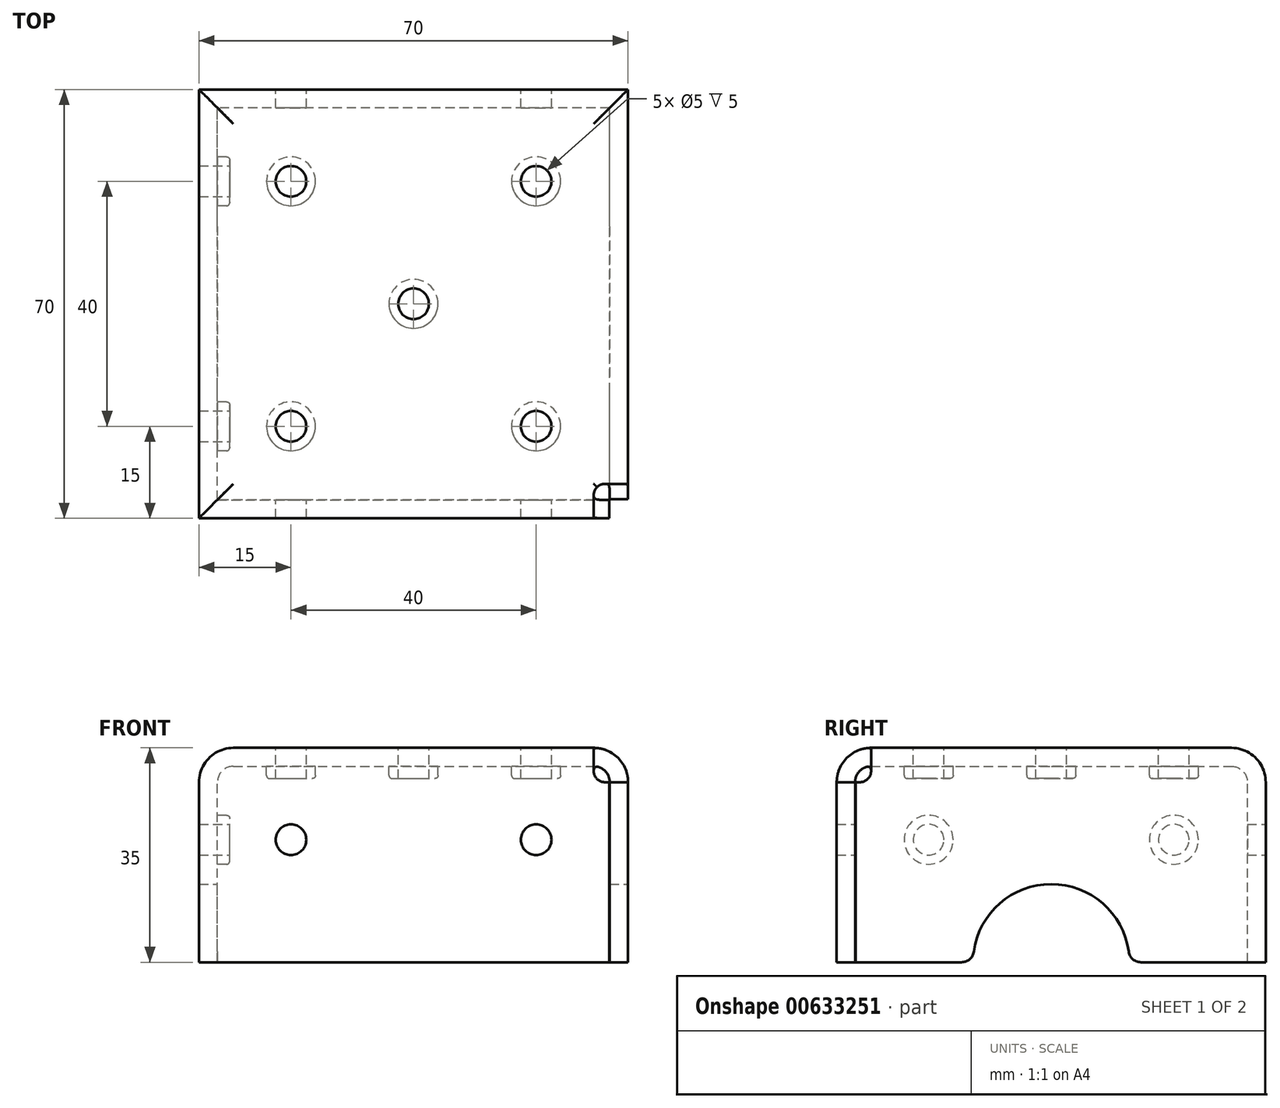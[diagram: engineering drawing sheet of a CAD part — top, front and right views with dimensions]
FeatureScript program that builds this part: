
annotation { "Feature Type Name" : "Feature", "Feature Type Description" : "" }
export const myFeature = defineFeature(function(context is Context, id is Id, definition is map)
    precondition{}
    {
        {
            var Q0;
            Q0=qCreatedBy(makeId("Top.planeOp"),FACE);
            var sketch = newSketch(context, id + "F0", { "sketchPlane" : qUnion([Q0])});
            skLineSegment(sketch, "E0.bottom", {"start": v(35, -35) * mm, "end": v(-35, -35) * mm});
            skLineSegment(sketch, "E0.top", {"start": v(35, 35) * mm, "end": v(-35, 35) * mm});
            skLineSegment(sketch, "E0.left", {"start": v(35, -35) * mm, "end": v(35, 35) * mm});
            skLineSegment(sketch, "E0.right", {"start": v(-35, -35) * mm, "end": v(-35, 35) * mm});
            skPoint(sketch, "E0.middle", {"position": v(0, 0) * mm});
            skSolve(sketch);
        }
        {
            var Q0;
            Q0=qSketchRegion(id+"F0",true);
            extrude(context, id + "F1", {"entities" : qUnion([Q0]), "oppositeDirection" : true, "depth" : 35 * mm});
        }
        {
            var Q0;
            Q0=makeQuery(id+"F1.opExtrude","CAP_EDGE",EDGE,{"disambiguationData":[OSD([sQuery(id+"F0.wireOp",EDGE,"E0.bottom")])],"isStart":true});
            var Q1;
            Q1=makeQuery(id+"F1.opExtrude","CAP_EDGE",EDGE,{"disambiguationData":[OSD([sQuery(id+"F0.wireOp",EDGE,"E0.left")])],"isStart":true});
            var Q2;
            Q2=makeQuery(id+"F1.opExtrude","CAP_EDGE",EDGE,{"disambiguationData":[OSD([sQuery(id+"F0.wireOp",EDGE,"E0.top")])],"isStart":true});
            var Q3;
            Q3=makeQuery(id+"F1.opExtrude","CAP_EDGE",EDGE,{"disambiguationData":[OSD([sQuery(id+"F0.wireOp",EDGE,"E0.right")])],"isStart":true});
            fillet(context, id + "F2", {"entities" : qUnion([Q0, Q1, Q2, Q3]), "radius" : 5.6 * mm, "tangentPropagation" : true, "allowEdgeOverflow" : false});
        }
        {
            var Q0;
            Q0=makeQuery(id+"F1.opExtrude","CAP_FACE",FACE,{"disambiguationData":[OSD([sQuery(id+"F0.wireOp",EDGE,"E0.bottom"),sQuery(id+"F0.wireOp",EDGE,"E0.top"),sQuery(id+"F0.wireOp",EDGE,"E0.left"),sQuery(id+"F0.wireOp",EDGE,"E0.right")])],"isStart":false});
            shell(context, id + "F3", {"entities" : qUnion([Q0]), "thickness" : 3 * mm});
        }
        {
            var Q0;
            Q0=makeQuery(id+"F1.opExtrude","CAP_FACE",FACE,{"disambiguationData":[OSD([sQuery(id+"F0.wireOp",EDGE,"E0.bottom"),sQuery(id+"F0.wireOp",EDGE,"E0.top"),sQuery(id+"F0.wireOp",EDGE,"E0.left"),sQuery(id+"F0.wireOp",EDGE,"E0.right")])],"isStart":false});
            var sketch = newSketch(context, id + "F4", { "sketchPlane" : qUnion([Q0])});
            skLineSegment(sketch, "E1.bottom", {"start": v(35, 35) * mm, "end": v(31.9, 35) * mm});
            skLineSegment(sketch, "E1.top", {"start": v(35, 31.9) * mm, "end": v(31.9, 31.9) * mm});
            skLineSegment(sketch, "E1.left", {"start": v(35, 35) * mm, "end": v(35, 31.9) * mm});
            skLineSegment(sketch, "E1.right", {"start": v(31.9, 35) * mm, "end": v(31.9, 31.9) * mm});
            skSolve(sketch);
        }
        {
            var Q0;
            Q0=qSketchRegion(id+"F4",true);
            extrude(context, id + "F5", {"entities" : qUnion([Q0]), "operationType" : NewBodyOperationType.REMOVE, "oppositeDirection" : true, "depth" : 38.4 * mm});
        }
        {
            var Q0;
            Q0=makeQuery(id+"F1.opExtrude","CAP_FACE",FACE,{"disambiguationData":[OSD([sQuery(id+"F0.wireOp",EDGE,"E0.bottom"),sQuery(id+"F0.wireOp",EDGE,"E0.top"),sQuery(id+"F0.wireOp",EDGE,"E0.left"),sQuery(id+"F0.wireOp",EDGE,"E0.right")])],"isStart":true});
            var sketch = newSketch(context, id + "F6", { "sketchPlane" : qUnion([Q0])});
            skLineSegment(sketch, "E2.bottom", {"start": v(29.4, -29.4) * mm, "end": v(35, -29.4) * mm});
            skLineSegment(sketch, "E2.top", {"start": v(29.4, -35) * mm, "end": v(35, -35) * mm});
            skLineSegment(sketch, "E2.left", {"start": v(29.4, -29.4) * mm, "end": v(29.4, -35) * mm});
            skLineSegment(sketch, "E2.right", {"start": v(35, -29.4) * mm, "end": v(35, -35) * mm});
            skSolve(sketch);
        }
        {
            var Q0;
            Q0=makeQuery(id+"F6.imprint","IMPRINT",FACE,{"disambiguationData":[TD([[makeQuery(id+"F6.imprint","IMPRINT",EDGE,{"derivedFrom":sQuery(id+"F6.wireOp",EDGE,"E2.bottom")}),-1.0]])]});
            extrude(context, id + "F7", {"entities" : qUnion([Q0]), "operationType" : NewBodyOperationType.REMOVE, "oppositeDirection" : true, "depth" : 5.6 * mm});
        }
        {
            var Q0;
            Q0=makeQuery(id+"F7.boolean.opBoolean","COPY",EDGE,{"derivedFrom":makeQuery(id+"F7.opExtrude","SWEPT_EDGE",EDGE,{"disambiguationData":[OSD([sQuery(id+"F0.wireOp",EDGE,"E0.bottom"),sQuery(id+"F0.wireOp",EDGE,"E0.top"),sQuery(id+"F0.wireOp",EDGE,"E0.left"),sQuery(id+"F0.wireOp",EDGE,"E0.right"),sQuery(id+"F6.wireOp",EDGE,"E2.bottom"),sQuery(id+"F6.wireOp",EDGE,"E2.left")])]})});
            var Q1;
            Q1=makeQuery(id+"F7.boolean.opBoolean","COPY",EDGE,{"derivedFrom":makeQuery(id+"F7.opExtrude","CAP_EDGE",EDGE,{"disambiguationData":[OSD([sQuery(id+"F6.wireOp",EDGE,"E2.bottom")])],"isStart":false})});
            var Q2;
            Q2=makeQuery(id+"F7.boolean.opBoolean","COPY",EDGE,{"derivedFrom":makeQuery(id+"F7.opExtrude","CAP_EDGE",EDGE,{"disambiguationData":[OSD([sQuery(id+"F6.wireOp",EDGE,"E2.left")])],"isStart":false})});
            fillet(context, id + "F8", {"entities" : qUnion([Q0, Q1, Q2]), "radius" : 1.8 * mm, "tangentPropagation" : true, "allowEdgeOverflow" : false});
        }
        {
            var Q0;
            Q0=makeQuery(id+"F3.opShell","OFFSET_FACE",FACE,{"disambiguationData":[OSD([sQuery(id+"F0.wireOp",EDGE,"E0.bottom"),sQuery(id+"F0.wireOp",EDGE,"E0.top"),sQuery(id+"F0.wireOp",EDGE,"E0.left"),sQuery(id+"F0.wireOp",EDGE,"E0.right")])]});
            var sketch = newSketch(context, id + "F9", { "sketchPlane" : qUnion([Q0])});
            skCircle(sketch, "E3", {"center": v(-20, 20) * mm, "radius": 4 * mm});
            skLineSegment(sketch, "E4.bottom", {"start": v(-20, 20) * mm, "end": v(20, 20) * mm, "construction": true});
            skLineSegment(sketch, "E4.top", {"start": v(-20, -20) * mm, "end": v(20, -20) * mm, "construction": true});
            skLineSegment(sketch, "E4.left", {"start": v(-20, 20) * mm, "end": v(-20, -20) * mm, "construction": true});
            skLineSegment(sketch, "E4.right", {"start": v(20, 20) * mm, "end": v(20, -20) * mm, "construction": true});
            skPoint(sketch, "E4.middle", {"position": v(0, 0) * mm});
            skCircle(sketch, "E5", {"center": v(-20, -20) * mm, "radius": 4 * mm});
            skCircle(sketch, "E6", {"center": v(20, -20) * mm, "radius": 4 * mm});
            skCircle(sketch, "E7", {"center": v(20, 20) * mm, "radius": 4 * mm});
            skCircle(sketch, "E8", {"center": v(0, 0) * mm, "radius": 4 * mm});
            skSolve(sketch);
        }
        {
            var Q0;
            Q0=makeQuery(id+"F9.imprint","IMPRINT",FACE,{"disambiguationData":[TD([[makeQuery(id+"F9.imprint","IMPRINT",EDGE,{"derivedFrom":sQuery(id+"F9.wireOp",EDGE,"E5")}),1.0]])]});
            var Q1;
            Q1=makeQuery(id+"F9.imprint","IMPRINT",FACE,{"disambiguationData":[TD([[makeQuery(id+"F9.imprint","IMPRINT",EDGE,{"derivedFrom":sQuery(id+"F9.wireOp",EDGE,"E6")}),1.0]])]});
            var Q2;
            Q2=makeQuery(id+"F9.imprint","IMPRINT",FACE,{"disambiguationData":[TD([[makeQuery(id+"F9.imprint","IMPRINT",EDGE,{"derivedFrom":sQuery(id+"F9.wireOp",EDGE,"E7")}),1.0]])]});
            var Q3;
            Q3=makeQuery(id+"F9.imprint","IMPRINT",FACE,{"disambiguationData":[TD([[makeQuery(id+"F9.imprint","IMPRINT",EDGE,{"derivedFrom":sQuery(id+"F9.wireOp",EDGE,"E3")}),1.0]])]});
            var Q4;
            Q4=makeQuery(id+"F9.imprint","IMPRINT",FACE,{"disambiguationData":[TD([[makeQuery(id+"F9.imprint","IMPRINT",EDGE,{"derivedFrom":sQuery(id+"F9.wireOp",EDGE,"E8")}),1.0]])]});
            extrude(context, id + "F10", {"entities" : qUnion([Q0, Q1, Q2, Q3, Q4]), "operationType" : NewBodyOperationType.ADD, "depth" : 2 * mm});
        }
        {
            var Q0;
            Q0=makeQuery(id+"F10.opExtrude","CAP_EDGE",EDGE,{"disambiguationData":[OSD([sQuery(id+"F9.wireOp",EDGE,"E3")])],"isStart":false});
            var Q1;
            Q1=makeQuery(id+"F10.opExtrude","CAP_EDGE",EDGE,{"disambiguationData":[OSD([sQuery(id+"F9.wireOp",EDGE,"E3")])],"isStart":true});
            var Q2;
            Q2=makeQuery(id+"F10.opExtrude","CAP_FACE",FACE,{"disambiguationData":[OSD([sQuery(id+"F9.wireOp",EDGE,"E5")])],"isStart":false});
            var Q3;
            Q3=makeQuery(id+"F10.opExtrude","CAP_FACE",FACE,{"disambiguationData":[OSD([sQuery(id+"F9.wireOp",EDGE,"E6")])],"isStart":false});
            var Q4;
            Q4=makeQuery(id+"F10.opExtrude","CAP_FACE",FACE,{"disambiguationData":[OSD([sQuery(id+"F9.wireOp",EDGE,"E7")])],"isStart":false});
            var Q5;
            Q5=makeQuery(id+"F10.opExtrude","CAP_EDGE",EDGE,{"disambiguationData":[OSD([sQuery(id+"F9.wireOp",EDGE,"E5")])],"isStart":true});
            var Q6;
            Q6=makeQuery(id+"F10.opExtrude","CAP_EDGE",EDGE,{"disambiguationData":[OSD([sQuery(id+"F9.wireOp",EDGE,"E6")])],"isStart":true});
            var Q7;
            Q7=makeQuery(id+"F10.opExtrude","CAP_EDGE",EDGE,{"disambiguationData":[OSD([sQuery(id+"F9.wireOp",EDGE,"E7")])],"isStart":true});
            var Q8;
            Q8=makeQuery(id+"F10.opExtrude","CAP_EDGE",EDGE,{"disambiguationData":[OSD([sQuery(id+"F9.wireOp",EDGE,"E8")])],"isStart":true});
            var Q9;
            Q9=makeQuery(id+"F10.opExtrude","CAP_EDGE",EDGE,{"disambiguationData":[OSD([sQuery(id+"F9.wireOp",EDGE,"E8")])],"isStart":false});
            fillet(context, id + "F11", {"entities" : qUnion([Q0, Q1, Q2, Q3, Q4, Q5, Q6, Q7, Q8, Q9]), "radius" : 0.5 * mm, "tangentPropagation" : true, "allowEdgeOverflow" : false});
        }
        {
            var Q0;
            Q0=makeQuery(id+"F1.opExtrude","CAP_FACE",FACE,{"disambiguationData":[OSD([sQuery(id+"F0.wireOp",EDGE,"E0.bottom"),sQuery(id+"F0.wireOp",EDGE,"E0.top"),sQuery(id+"F0.wireOp",EDGE,"E0.left"),sQuery(id+"F0.wireOp",EDGE,"E0.right")])],"isStart":true});
            var sketch = newSketch(context, id + "F12", { "sketchPlane" : qUnion([Q0])});
            skCircle(sketch, "E9.0", {"center": v(-20, -20) * mm, "radius": 3.5 * mm, "construction": true});
            skCircle(sketch, "E10.0", {"center": v(-20, 20) * mm, "radius": 3.5 * mm, "construction": true});
            skCircle(sketch, "E11.0", {"center": v(20, 20) * mm, "radius": 3.5 * mm, "construction": true});
            skCircle(sketch, "E12.0", {"center": v(20, -20) * mm, "radius": 3.5 * mm, "construction": true});
            skCircle(sketch, "E13.0", {"center": v(0, 0) * mm, "radius": 3.5 * mm, "construction": true});
            skSolve(sketch);
        }
        {
            var Q0;
            Q0=sQuery(id+"F12.wireOp",VERTEX,"E9.0.center");
            var Q1;
            Q1=sQuery(id+"F12.wireOp",VERTEX,"E10.0.center");
            var Q2;
            Q2=sQuery(id+"F12.wireOp",VERTEX,"E11.0.center");
            var Q3;
            Q3=sQuery(id+"F12.wireOp",VERTEX,"E13.0.center");
            var Q4;
            Q4=sQuery(id+"F12.wireOp",VERTEX,"E12.0.center");
            var Q5;
            Q5=makeQuery(id+"F1.opExtrude","SWEPT_BODY",BODY,{"disambiguationData":[OSD([sQuery(id+"F0.wireOp",EDGE,"E0.bottom"),sQuery(id+"F0.wireOp",EDGE,"E0.top"),sQuery(id+"F0.wireOp",EDGE,"E0.left"),sQuery(id+"F0.wireOp",EDGE,"E0.right")])]});
            hole(context, id + "F13", {"style" : HoleStyle.SIMPLE, "endStyle" : HoleEndStyle.THROUGH, "standardTappedOrClearance" : lookupTablePath({ "standard" : "ISO", "engagement" : "75%", "pitch" : "1 mm", "size" : "M6", "type" : "Tapped" }), "standardBlindInLast" : lookupTablePath({ "standard" : "ISO", "engagement" : "75%", "pitch" : "1 mm", "size" : "M6", "type" : "Tapped" }), "holeDiameter" : 5 * mm, "locations" : qUnion([Q0, Q1, Q2, Q3, Q4]), "scope" : qUnion([Q5]), "isTappedThrough" : true, "majorDiameter" : 6 * mm, "showTappedDepth" : true});
        }
        {
            var Q0;
            {var subQ0=sQuery(id+"F0.wireOp",EDGE,"E0.right");Q0=makeQuery(id+"F3.opShell","OFFSET_FACE",FACE,{"disambiguationData":[OSD([subQ0]),TDD([makeQuery(id+"F1.opExtrude","SWEPT_FACE",FACE,{"disambiguationData":[OSD([subQ0])]})])]});}
            var sketch = newSketch(context, id + "F14", { "sketchPlane" : qUnion([Q0])});
            skCircle(sketch, "E14", {"center": v(-20, -15) * mm, "radius": 4 * mm});
            skCircle(sketch, "E15", {"center": v(20, -15) * mm, "radius": 4 * mm});
            skSolve(sketch);
        }
        {
            var Q0;
            Q0=qSketchRegion(id+"F14",true);
            extrude(context, id + "F15", {"entities" : qUnion([Q0]), "operationType" : NewBodyOperationType.ADD, "depth" : 2 * mm});
        }
        {
            var Q0;
            Q0=makeQuery(id+"F15.opExtrude","CAP_EDGE",EDGE,{"disambiguationData":[OSD([sQuery(id+"F14.wireOp",EDGE,"E14")])],"isStart":false});
            var Q1;
            Q1=makeQuery(id+"F15.opExtrude","CAP_EDGE",EDGE,{"disambiguationData":[OSD([sQuery(id+"F14.wireOp",EDGE,"E15")])],"isStart":false});
            var Q2;
            Q2=makeQuery(id+"F15.opExtrude","CAP_EDGE",EDGE,{"disambiguationData":[OSD([sQuery(id+"F14.wireOp",EDGE,"E15")])],"isStart":true});
            var Q3;
            Q3=makeQuery(id+"F15.opExtrude","CAP_EDGE",EDGE,{"disambiguationData":[OSD([sQuery(id+"F14.wireOp",EDGE,"E14")])],"isStart":true});
            fillet(context, id + "F16", {"entities" : qUnion([Q0, Q1, Q2, Q3]), "radius" : 0.5 * mm, "tangentPropagation" : true, "allowEdgeOverflow" : false});
        }
        {
            var Q0;
            Q0=makeQuery(id+"F15.opExtrude","CAP_FACE",FACE,{"disambiguationData":[OSD([sQuery(id+"F14.wireOp",EDGE,"E14")])],"isStart":false});
            var sketch = newSketch(context, id + "F17", { "sketchPlane" : qUnion([Q0])});
            skPoint(sketch, "E16", {"position": v(-20, -15) * mm});
            skPoint(sketch, "E17", {"position": v(20, -15) * mm});
            skSolve(sketch);
        }
        {
            var Q0;
            Q0=sQuery(id+"F17.wireOp",VERTEX,"E16");
            var Q1;
            Q1=sQuery(id+"F17.wireOp",VERTEX,"E17");
            var Q2;
            Q2=makeQuery(id+"F1.opExtrude","SWEPT_BODY",BODY,{"disambiguationData":[OSD([sQuery(id+"F0.wireOp",EDGE,"E0.bottom"),sQuery(id+"F0.wireOp",EDGE,"E0.top"),sQuery(id+"F0.wireOp",EDGE,"E0.left"),sQuery(id+"F0.wireOp",EDGE,"E0.right")])]});
            hole(context, id + "F18", {"style" : HoleStyle.SIMPLE, "endStyle" : HoleEndStyle.THROUGH, "standardTappedOrClearance" : lookupTablePath({ "standard" : "ISO", "engagement" : "75%", "pitch" : "1 mm", "size" : "M6", "type" : "Tapped" }), "standardBlindInLast" : lookupTablePath({ "standard" : "ISO", "engagement" : "75%", "pitch" : "1 mm", "size" : "M6", "type" : "Tapped" }), "holeDiameter" : 5 * mm, "locations" : qUnion([Q0, Q1]), "scope" : qUnion([Q2]), "isTappedThrough" : true, "majorDiameter" : 6 * mm, "showTappedDepth" : true});
        }
        {
            var Q0;
            Q0=makeQuery(id+"F1.opExtrude","SWEPT_FACE",FACE,{"disambiguationData":[OSD([sQuery(id+"F0.wireOp",EDGE,"E0.top")])]});
            var sketch = newSketch(context, id + "F19", { "sketchPlane" : qUnion([Q0])});
            skPoint(sketch, "E18", {"position": v(-20, -15) * mm});
            skPoint(sketch, "E19", {"position": v(20, -15) * mm});
            skSolve(sketch);
        }
        {
            var Q0;
            Q0=sQuery(id+"F19.wireOp",VERTEX,"E19");
            var Q1;
            Q1=sQuery(id+"F19.wireOp",VERTEX,"E18");
            var Q2;
            Q2=makeQuery(id+"F1.opExtrude","SWEPT_BODY",BODY,{"disambiguationData":[OSD([sQuery(id+"F0.wireOp",EDGE,"E0.bottom"),sQuery(id+"F0.wireOp",EDGE,"E0.top"),sQuery(id+"F0.wireOp",EDGE,"E0.left"),sQuery(id+"F0.wireOp",EDGE,"E0.right")])]});
            hole(context, id + "F20", {"style" : HoleStyle.SIMPLE, "endStyle" : HoleEndStyle.THROUGH, "standardTappedOrClearance" : lookupTablePath({ "standard" : "ISO", "engagement" : "75%", "pitch" : "1 mm", "size" : "M6", "type" : "Tapped" }), "standardBlindInLast" : lookupTablePath({ "standard" : "ISO", "engagement" : "75%", "pitch" : "1 mm", "size" : "M6", "type" : "Tapped" }), "holeDiameter" : 5 * mm, "locations" : qUnion([Q0, Q1]), "scope" : qUnion([Q2]), "isTappedThrough" : true, "majorDiameter" : 6 * mm, "showTappedDepth" : true});
        }
        {
            var Q0;
            Q0=makeQuery(id+"F1.opExtrude","SWEPT_FACE",FACE,{"disambiguationData":[OSD([sQuery(id+"F0.wireOp",EDGE,"E0.bottom")])]});
            var sketch = newSketch(context, id + "F21", { "sketchPlane" : qUnion([Q0])});
            skCircle(sketch, "E20", {"center": v(0, -35) * mm, "radius": 15.25 * mm});
            skSolve(sketch);
        }
        {
            var Q0;
            {var subQ0=sQuery(id+"F21.wireOp",EDGE,"E20");var subQ1=makeQuery(id+"F1.opExtrude","CAP_EDGE",EDGE,{"disambiguationData":[OSD([sQuery(id+"F0.wireOp",EDGE,"E0.bottom")])],"isStart":false});var subQ2=makeQuery(id+"F21.imprint","INTERSECT",VERTEX,{"disambiguationData":[OD(0.0)],"derivedFrom":[subQ1,subQ0]});Q0=makeQuery(id+"F21.imprint","IMPRINT",FACE,{"disambiguationData":[TD([[makeQuery(id+"F21.imprint","IMPRINT",EDGE,{"disambiguationData":[TD([[subQ2,-1.0]])],"derivedFrom":subQ0}),1.0]])]});}
            extrude(context, id + "F22", {"entities" : qUnion([Q0]), "operationType" : NewBodyOperationType.REMOVE, "endBound" : BoundingType.THROUGH_ALL, "oppositeDirection" : true, "depth" : 25 * mm});
        }
        {
            var Q0;
            Q0=makeQuery(id+"F1.opExtrude","SWEPT_FACE",FACE,{"disambiguationData":[OSD([sQuery(id+"F0.wireOp",EDGE,"E0.left")])]});
            var sketch = newSketch(context, id + "F23", { "sketchPlane" : qUnion([Q0])});
            skCircle(sketch, "E21", {"center": v(0, -35) * mm, "radius": 12.75 * mm});
            skSolve(sketch);
        }
        {
            var Q0;
            Q0=qSketchRegion(id+"F23",true);
            extrude(context, id + "F24", {"entities" : qUnion([Q0]), "operationType" : NewBodyOperationType.REMOVE, "endBound" : BoundingType.THROUGH_ALL, "oppositeDirection" : true, "depth" : 25 * mm});
        }
        {
            var Q0;
            {var subQ0=sQuery(id+"F0.wireOp",EDGE,"E0.bottom");var subQ1=makeQuery(id+"F1.opExtrude","SWEPT_FACE",FACE,{"disambiguationData":[OSD([subQ0])]});var subQ2=sQuery(id+"F21.wireOp",EDGE,"E20");Q0=makeQuery(id+"F22.boolean.opBoolean","COPY",EDGE,{"disambiguationData":[TD([subQ1])],"derivedFrom":makeQuery(id+"F22.opExtrude","SWEPT_EDGE",EDGE,{"disambiguationData":[OSD([subQ0,subQ2]),TDD([makeQuery(id+"F21.imprint","INTERSECT",VERTEX,{"disambiguationData":[OD(0.0)],"derivedFrom":[makeQuery(id+"F1.opExtrude","CAP_EDGE",EDGE,{"disambiguationData":[OSD([subQ0])],"isStart":false}),subQ2]})])]})});}
            var Q1;
            {var subQ0=sQuery(id+"F0.wireOp",EDGE,"E0.bottom");var subQ1=makeQuery(id+"F1.opExtrude","SWEPT_FACE",FACE,{"disambiguationData":[OSD([subQ0])]});var subQ2=sQuery(id+"F21.wireOp",EDGE,"E20");Q1=makeQuery(id+"F22.boolean.opBoolean","COPY",EDGE,{"disambiguationData":[TD([subQ1])],"derivedFrom":makeQuery(id+"F22.opExtrude","SWEPT_EDGE",EDGE,{"disambiguationData":[OSD([subQ0,subQ2]),TDD([makeQuery(id+"F21.imprint","INTERSECT",VERTEX,{"disambiguationData":[OD(1.0)],"derivedFrom":[makeQuery(id+"F1.opExtrude","CAP_EDGE",EDGE,{"disambiguationData":[OSD([subQ0])],"isStart":false}),subQ2]})])]})});}
            var Q2;
            {var subQ0=sQuery(id+"F0.wireOp",EDGE,"E0.right");var subQ1=makeQuery(id+"F1.opExtrude","SWEPT_FACE",FACE,{"disambiguationData":[OSD([subQ0])]});var subQ6=sQuery(id+"F0.wireOp",EDGE,"E0.top");var subQ7=makeQuery(id+"F1.opExtrude","SWEPT_FACE",FACE,{"disambiguationData":[OSD([subQ6])]});var subQ9=sQuery(id+"F0.wireOp",EDGE,"E0.left");Q2=makeQuery(id+"F24.boolean.opBoolean","INTERSECT",EDGE,{"disambiguationData":[OD(0.0)],"derivedFrom":[makeQuery(id+"Fg5Al07xBOhborq_1.1.FdxJJ5X4k0Y0wya_1.1.F5.boolean.opBoolean","SPLIT",FACE,{"disambiguationData":[TD([subQ1])],"derivedFrom":makeQuery(id+"Fg5Al07xBOhborq_1.1.F5.boolean.opBoolean","SPLIT",FACE,{"disambiguationData":[TD([subQ7])],"derivedFrom":makeQuery(id+"FdxJJ5X4k0Y0wya_1.1.F5.boolean.opBoolean","SPLIT",FACE,{"disambiguationData":[TD([subQ7])],"derivedFrom":makeQuery(id+"F1.opExtrude","CAP_FACE",FACE,{"disambiguationData":[OSD([sQuery(id+"F0.wireOp",EDGE,"E0.bottom"),subQ6,subQ9,subQ0])],"isStart":false})})})}),makeQuery(id+"F24.opExtrude","SWEPT_FACE",FACE,{"disambiguationData":[OSD([sQuery(id+"F23.wireOp",EDGE,"E21")])]})]});}
            var Q3;
            {var subQ0=sQuery(id+"F0.wireOp",EDGE,"E0.right");var subQ1=makeQuery(id+"F1.opExtrude","SWEPT_FACE",FACE,{"disambiguationData":[OSD([subQ0])]});var subQ6=sQuery(id+"F0.wireOp",EDGE,"E0.top");var subQ7=makeQuery(id+"F1.opExtrude","SWEPT_FACE",FACE,{"disambiguationData":[OSD([subQ6])]});var subQ9=sQuery(id+"F0.wireOp",EDGE,"E0.left");Q3=makeQuery(id+"F24.boolean.opBoolean","INTERSECT",EDGE,{"disambiguationData":[OD(1.0)],"derivedFrom":[makeQuery(id+"Fg5Al07xBOhborq_1.1.FdxJJ5X4k0Y0wya_1.1.F5.boolean.opBoolean","SPLIT",FACE,{"disambiguationData":[TD([subQ1])],"derivedFrom":makeQuery(id+"Fg5Al07xBOhborq_1.1.F5.boolean.opBoolean","SPLIT",FACE,{"disambiguationData":[TD([subQ7])],"derivedFrom":makeQuery(id+"FdxJJ5X4k0Y0wya_1.1.F5.boolean.opBoolean","SPLIT",FACE,{"disambiguationData":[TD([subQ7])],"derivedFrom":makeQuery(id+"F1.opExtrude","CAP_FACE",FACE,{"disambiguationData":[OSD([sQuery(id+"F0.wireOp",EDGE,"E0.bottom"),subQ6,subQ9,subQ0])],"isStart":false})})})}),makeQuery(id+"F24.opExtrude","SWEPT_FACE",FACE,{"disambiguationData":[OSD([sQuery(id+"F23.wireOp",EDGE,"E21")])]})]});}
            var Q4;
            Q4=makeQuery(id+"Fg5Al07xBOhborq_1.1.FdxJJ5X4k0Y0wya_1.1.F5.boolean.opBoolean","COPY",EDGE,{"derivedFrom":makeQuery(id+"Fg5Al07xBOhborq_1.1.FdxJJ5X4k0Y0wya_1.1.F5.opExtrude","CAP_EDGE",EDGE,{"disambiguationData":[OSD([sQuery(id+"F4.wireOp",EDGE,"E1.top")])],"isStart":true})});
            var Q5;
            Q5=makeQuery(id+"Fg5Al07xBOhborq_1.1.FdxJJ5X4k0Y0wya_1.1.F5.boolean.opBoolean","COPY",EDGE,{"derivedFrom":makeQuery(id+"Fg5Al07xBOhborq_1.1.FdxJJ5X4k0Y0wya_1.1.F5.opExtrude","CAP_EDGE",EDGE,{"disambiguationData":[OSD([sQuery(id+"F4.wireOp",EDGE,"E1.right")])],"isStart":true})});
            var Q6;
            {var subQ0=sQuery(id+"F0.wireOp",EDGE,"E0.top");var subQ1=sQuery(id+"F0.wireOp",EDGE,"E0.bottom");var subQ2=makeQuery(id+"F1.opExtrude","SWEPT_FACE",FACE,{"disambiguationData":[OSD([subQ0])]});var subQ3=sQuery(id+"F21.wireOp",EDGE,"E20");Q6=makeQuery(id+"F22.boolean.opBoolean","COPY",EDGE,{"disambiguationData":[TD([subQ2])],"derivedFrom":makeQuery(id+"F22.opExtrude","SWEPT_EDGE",EDGE,{"disambiguationData":[OSD([subQ1,subQ3]),TDD([makeQuery(id+"F21.imprint","INTERSECT",VERTEX,{"disambiguationData":[OD(1.0)],"derivedFrom":[makeQuery(id+"F1.opExtrude","CAP_EDGE",EDGE,{"disambiguationData":[OSD([subQ1])],"isStart":false}),subQ3]})])]})});}
            var Q7;
            {var subQ0=sQuery(id+"F0.wireOp",EDGE,"E0.top");var subQ1=sQuery(id+"F0.wireOp",EDGE,"E0.bottom");var subQ2=makeQuery(id+"F1.opExtrude","SWEPT_FACE",FACE,{"disambiguationData":[OSD([subQ0])]});var subQ3=sQuery(id+"F21.wireOp",EDGE,"E20");Q7=makeQuery(id+"F22.boolean.opBoolean","COPY",EDGE,{"disambiguationData":[TD([subQ2])],"derivedFrom":makeQuery(id+"F22.opExtrude","SWEPT_EDGE",EDGE,{"disambiguationData":[OSD([subQ1,subQ3]),TDD([makeQuery(id+"F21.imprint","INTERSECT",VERTEX,{"disambiguationData":[OD(0.0)],"derivedFrom":[makeQuery(id+"F1.opExtrude","CAP_EDGE",EDGE,{"disambiguationData":[OSD([subQ1])],"isStart":false}),subQ3]})])]})});}
            var Q8;
            {var subQ0=sQuery(id+"F0.wireOp",EDGE,"E0.left");var subQ1=makeQuery(id+"F1.opExtrude","SWEPT_FACE",FACE,{"disambiguationData":[OSD([subQ0])]});var subQ5=sQuery(id+"F0.wireOp",EDGE,"E0.top");var subQ6=makeQuery(id+"F1.opExtrude","SWEPT_FACE",FACE,{"disambiguationData":[OSD([subQ5])]});var subQ7=sQuery(id+"F0.wireOp",EDGE,"E0.right");Q8=makeQuery(id+"F24.boolean.opBoolean","INTERSECT",EDGE,{"disambiguationData":[OD(1.0)],"derivedFrom":[makeQuery(id+"Fg5Al07xBOhborq_1.1.F5.boolean.opBoolean","SPLIT",FACE,{"disambiguationData":[TD([subQ1])],"derivedFrom":makeQuery(id+"FdxJJ5X4k0Y0wya_1.1.F5.boolean.opBoolean","SPLIT",FACE,{"disambiguationData":[TD([subQ6])],"derivedFrom":makeQuery(id+"F1.opExtrude","CAP_FACE",FACE,{"disambiguationData":[OSD([sQuery(id+"F0.wireOp",EDGE,"E0.bottom"),subQ5,subQ0,subQ7])],"isStart":false})})}),makeQuery(id+"F24.opExtrude","SWEPT_FACE",FACE,{"disambiguationData":[OSD([sQuery(id+"F23.wireOp",EDGE,"E21")])]})]});}
            var Q9;
            {var subQ0=sQuery(id+"F0.wireOp",EDGE,"E0.left");var subQ1=makeQuery(id+"F1.opExtrude","SWEPT_FACE",FACE,{"disambiguationData":[OSD([subQ0])]});var subQ5=sQuery(id+"F0.wireOp",EDGE,"E0.top");var subQ6=makeQuery(id+"F1.opExtrude","SWEPT_FACE",FACE,{"disambiguationData":[OSD([subQ5])]});var subQ7=sQuery(id+"F0.wireOp",EDGE,"E0.right");Q9=makeQuery(id+"F24.boolean.opBoolean","INTERSECT",EDGE,{"disambiguationData":[OD(0.0)],"derivedFrom":[makeQuery(id+"Fg5Al07xBOhborq_1.1.F5.boolean.opBoolean","SPLIT",FACE,{"disambiguationData":[TD([subQ1])],"derivedFrom":makeQuery(id+"FdxJJ5X4k0Y0wya_1.1.F5.boolean.opBoolean","SPLIT",FACE,{"disambiguationData":[TD([subQ6])],"derivedFrom":makeQuery(id+"F1.opExtrude","CAP_FACE",FACE,{"disambiguationData":[OSD([sQuery(id+"F0.wireOp",EDGE,"E0.bottom"),subQ5,subQ0,subQ7])],"isStart":false})})}),makeQuery(id+"F24.opExtrude","SWEPT_FACE",FACE,{"disambiguationData":[OSD([sQuery(id+"F23.wireOp",EDGE,"E21")])]})]});}
            fillet(context, id + "F25", {"entities" : qUnion([Q0, Q1, Q2, Q3, Q4, Q5, Q6, Q7, Q8, Q9]), "radius" : 2 * mm, "tangentPropagation" : true, "allowEdgeOverflow" : false});
        }
    });
